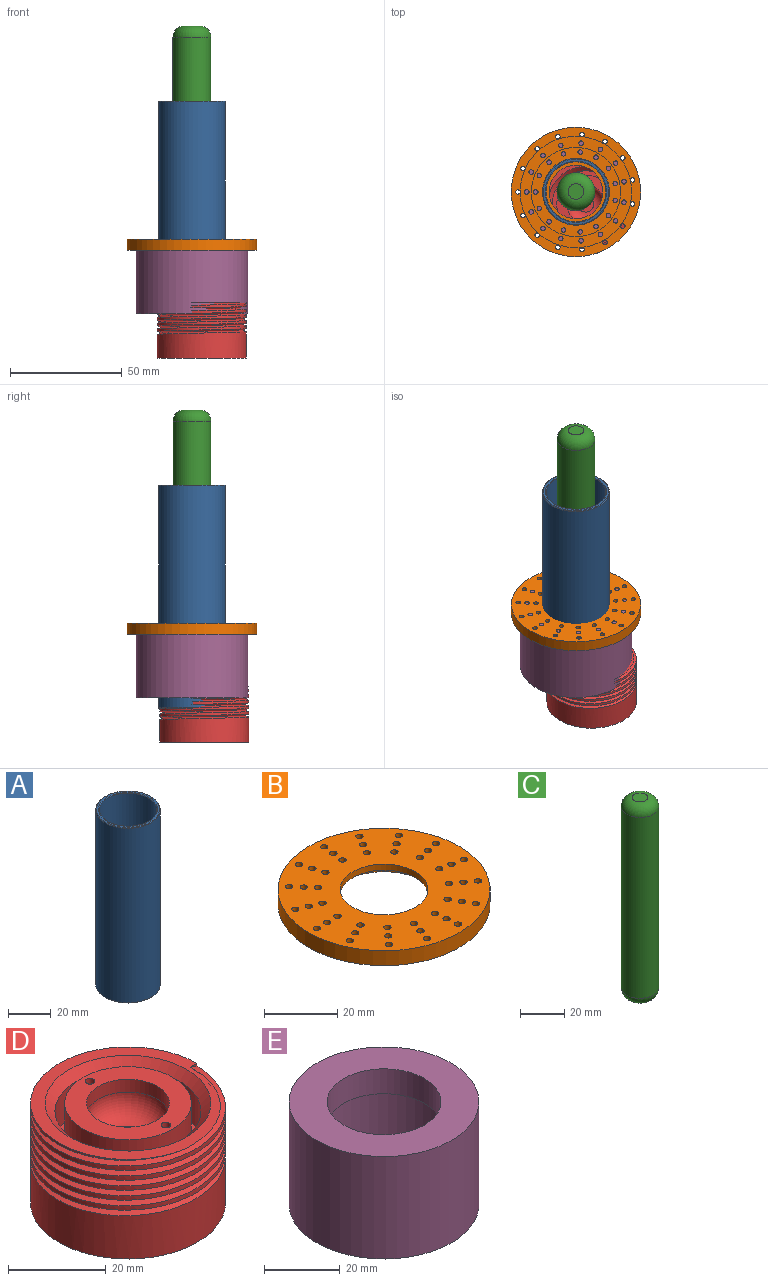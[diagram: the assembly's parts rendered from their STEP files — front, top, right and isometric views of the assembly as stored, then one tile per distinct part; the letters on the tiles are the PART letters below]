
ASSEMBLY  parts=5 mates=3
PART A: 8 faces, bbox 32.5x32.5x100 mm
  f0: cylinder r=13.4mm len=99.4mm, axis (0,0,-1), area 8369mm2, adj f4,f6
  f1: cylinder r=15mm len=99.4mm, axis (0,0,-1), area 9368.2mm2, adj f5,f7
  f2: plane 29.4x29.4mm, normal (0,0,1), area 89.2mm2, adj f6,f7
  f3: plane 29.4x29.4mm, normal (0,0,-1), area 89.2mm2, adj f4,f5
  f4: torus R=13.7mm, axis (0,0,1), area 40mm2, adj f0,f3
  f5: torus R=14.7mm, axis (0,0,1), area 44.1mm2, adj f1,f3
  f6: torus R=13.7mm, axis (0,0,1), area 40mm2, adj f0,f2
  f7: torus R=14.7mm, axis (0,0,1), area 44.1mm2, adj f1,f2
PART B: 51 faces, bbox 58x58x5 mm
  f0: cylinder r=12mm len=24mm, axis (0,0,1), area 150.8mm2, adj f2,f5
  f1: cylinder r=29mm len=58mm, axis (0,0,-1), area 911.1mm2, adj f2,f3
  f2: plane 58x58mm, normal (0,0,1), area 2048.3mm2, adj f0,f1,f6,f7,f8,f9,f10,f11
  f3: plane 58x58mm, normal (0,0,-1), area 1745.9mm2, adj f1,f4,f6,f7,f8,f9,f10,f11
  f4: cylinder r=15.5mm len=31mm, axis (0,0,-1), area 292.2mm2, adj f3,f5
  f5: plane 31x31mm, normal (0,0,-1), area 302.4mm2, adj f0,f4
  f6: cylinder r=1mm len=5mm, axis (0,0,1), area 31.4mm2, adj f2,f3
  f7: cylinder r=1mm len=5mm, axis (0,0,1), area 31.4mm2, adj f2,f3
  f8: cylinder r=1mm len=5mm, axis (0,0,1), area 31.4mm2, adj f2,f3
  f9: cylinder r=1mm len=5mm, axis (0,0,1), area 31.4mm2, adj f2,f3
  f10: cylinder r=1mm len=5mm, axis (0,0,1), area 31.4mm2, adj f2,f3
  f11: cylinder r=1mm len=5mm, axis (0,0,1), area 31.4mm2, adj f2,f3
  f12: cylinder r=1mm len=5mm, axis (0,0,1), area 31.4mm2, adj f2,f3
  f13: cylinder r=1mm len=5mm, axis (0,0,1), area 31.4mm2, adj f2,f3
  f14: cylinder r=1mm len=5mm, axis (0,0,1), area 31.4mm2, adj f2,f3
  f15: cylinder r=1mm len=5mm, axis (0,0,1), area 31.4mm2, adj f2,f3
  f16: cylinder r=1mm len=5mm, axis (0,0,1), area 31.4mm2, adj f2,f3
  f17: cylinder r=1mm len=5mm, axis (0,0,1), area 31.4mm2, adj f2,f3
  f18: cylinder r=1mm len=5mm, axis (0,0,1), area 31.4mm2, adj f2,f3
  f19: cylinder r=1mm len=5mm, axis (0,0,1), area 31.4mm2, adj f2,f3
  f20: cylinder r=1mm len=5mm, axis (0,0,1), area 31.4mm2, adj f2,f3
  f21: cylinder r=1mm len=5mm, axis (0,0,1), area 31.4mm2, adj f2,f3
  f22: cylinder r=1mm len=5mm, axis (0,0,1), area 31.4mm2, adj f2,f3
  f23: cylinder r=1mm len=5mm, axis (0,0,1), area 31.4mm2, adj f2,f3
  f24: cylinder r=1mm len=5mm, axis (0,0,1), area 31.4mm2, adj f2,f3
  f25: cylinder r=1mm len=5mm, axis (0,0,1), area 31.4mm2, adj f2,f3
  f26: cylinder r=1mm len=5mm, axis (0,0,1), area 31.4mm2, adj f2,f3
  f27: cylinder r=1mm len=5mm, axis (0,0,1), area 31.4mm2, adj f2,f3
  f28: cylinder r=1mm len=5mm, axis (0,0,1), area 31.4mm2, adj f2,f3
  f29: cylinder r=1mm len=5mm, axis (0,0,1), area 31.4mm2, adj f2,f3
  f30: cylinder r=1mm len=5mm, axis (0,0,1), area 31.4mm2, adj f2,f3
  f31: cylinder r=1mm len=5mm, axis (0,0,1), area 31.4mm2, adj f2,f3
  f32: cylinder r=1mm len=5mm, axis (0,0,1), area 31.4mm2, adj f2,f3
  f33: cylinder r=1mm len=5mm, axis (0,0,1), area 31.4mm2, adj f2,f3
  f34: cylinder r=1mm len=5mm, axis (0,0,1), area 31.4mm2, adj f2,f3
  f35: cylinder r=1mm len=5mm, axis (0,0,1), area 31.4mm2, adj f2,f3
  f36: cylinder r=1mm len=5mm, axis (0,0,1), area 31.4mm2, adj f2,f3
  f37: cylinder r=1mm len=5mm, axis (0,0,1), area 31.4mm2, adj f2,f3
  f38: cylinder r=1mm len=5mm, axis (0,0,1), area 31.4mm2, adj f2,f3
  f39: cylinder r=1mm len=5mm, axis (0,0,1), area 31.4mm2, adj f2,f3
  f40: cylinder r=1mm len=5mm, axis (0,0,1), area 31.4mm2, adj f2,f3
  f41: cylinder r=1mm len=5mm, axis (0,0,1), area 31.4mm2, adj f2,f3
  f42: cylinder r=1mm len=5mm, axis (0,0,1), area 31.4mm2, adj f2,f3
  f43: cylinder r=1mm len=5mm, axis (0,0,1), area 31.4mm2, adj f2,f3
  f44: cylinder r=1mm len=5mm, axis (0,0,1), area 31.4mm2, adj f2,f3
  f45: cylinder r=1mm len=5mm, axis (0,0,1), area 31.4mm2, adj f2,f3
  f46: cylinder r=1mm len=5mm, axis (0,0,1), area 31.4mm2, adj f2,f3
  f47: cylinder r=1mm len=5mm, axis (0,0,1), area 31.4mm2, adj f2,f3
  f48: cylinder r=1mm len=5mm, axis (0,0,1), area 31.4mm2, adj f2,f3
  f49: cylinder r=1mm len=5mm, axis (0,0,1), area 31.4mm2, adj f2,f3
  f50: cylinder r=1mm len=5mm, axis (0,0,1), area 31.4mm2, adj f2,f3
PART C: 7 faces, bbox 17x17x110 mm
  f0: cylinder r=8.5mm len=100mm, axis (0,0,-1), area 5340.7mm2, adj f3,f4
  f1: plane 7x7mm, normal (0,0,1), area 38.5mm2, adj f4
  f2: plane 7x7mm, normal (0,0,-1), area 33.6mm2, adj f3,f6
  f3: torus R=3.5mm, axis (0,0,1), area 329.8mm2, adj f0,f2
  f4: torus R=3.5mm, axis (0,0,1), area 329.8mm2, adj f0,f1
  f5: cone r=0mm half-angle=59deg, axis (0,0,-1), area 5.7mm2, adj f6
  f6: cylinder r=1.25mm len=6.5mm, axis (0,0,-1), area 51.1mm2, adj f2,f5
PART D: 27 faces, bbox 43.5x50.1x27.1 mm
  f0: cylinder r=20mm len=40mm, axis (0,0,-1), area 1327.1mm2, adj f1,f10,f23,f26
  f1: cylinder r=20mm len=40mm, axis (0,0,-1), area 138.9mm2, adj f0,f2,f25,f26
  f2: cylinder r=20mm len=40mm, axis (0,0,-1), area 138.7mm2, adj f1,f3,f25,f26
  f3: cylinder r=20mm len=40mm, axis (0,0,-1), area 138.8mm2, adj f2,f4,f25,f26
  f4: cylinder r=20mm len=40mm, axis (0,0,-1), area 139mm2, adj f3,f5,f25,f26
  f5: cylinder r=20mm len=40mm, axis (0,0,-1), area 138.8mm2, adj f4,f6,f25,f26
  f6: cylinder r=20mm len=40mm, axis (0,0,-1), area 81mm2, adj f5,f7,f24,f25
  f7: plane 40.94x40.75mm, normal (0,0,1), area 315.2mm2, adj f6,f18,f24,f25,f26
  f8: cylinder r=1mm len=16.94mm, axis (0,0,1), area 106.4mm2, adj f14,f21
  f9: cylinder r=1mm len=16.94mm, axis (0,0,1), area 106.4mm2, adj f14,f19
  f10: plane 40x40mm, normal (0,0,-1), area 1228.9mm2, adj f0,f20,f22
  f11: cylinder r=13mm len=26mm, axis (0,0,1), area 816.8mm2, adj f13,f14
  f12: cylinder r=15mm len=30mm, axis (0,0,1), area 754mm2, adj f13,f18
  f13: plane 30x30mm, normal (0,0,1), area 175.9mm2, adj f11,f12
  f14: plane 26x26mm, normal (0,0,1), area 297.7mm2, adj f8,f9,f11,f15
  f15: cylinder r=8.5mm len=17mm, axis (0,0,1), area 170.9mm2, adj f14,f17
  f16: plane 7x7mm, normal (0,0,1), area 38.5mm2, adj f17
  f17: torus R=3.5mm, axis (0,0,1), area 329.8mm2, adj f15,f16
  f18: cone r=15mm half-angle=45deg, axis (0,0,1), area 284.3mm2, adj f7,f12
  f19: cone r=0mm half-angle=59deg, axis (0,0,-1), area 12.5mm2, adj f9,f20
  f20: cylinder r=2.1mm len=7.4mm, axis (0,0,-1), area 97.6mm2, adj f10,f19
  f21: cone r=0mm half-angle=59deg, axis (0,0,-1), area 12.5mm2, adj f8,f22
  f22: cylinder r=2.1mm len=7.4mm, axis (0,0,-1), area 97.6mm2, adj f10,f21
  f23: plane 1.9x1.4mm, normal (0,1,0), area 1.3mm2, adj f0,f25,f26
  f24: plane 1.84x0.69mm, normal (0,-1,0), area 0.6mm2, adj f6,f7,f26
  f25: bspline ~49.18x42.59mm, area 1415.2mm2, adj f1,f2,f3,f4,f5,f6,f7,f23
  f26: bspline ~49.18x42.59mm, area 1456.3mm2, adj f0,f1,f2,f3,f4,f5,f7,f23
PART E: 6 faces, bbox 50x50x33 mm
  f0: cylinder r=20mm len=40mm, axis (0,0,-1), area 3141.6mm2, adj f2,f3
  f1: cylinder r=25mm len=50mm, axis (0,0,-1), area 5183.6mm2, adj f2,f5
  f2: plane 50x50mm, normal (0,0,-1), area 706.9mm2, adj f0,f1
  f3: plane 40x40mm, normal (0,0,-1), area 549.8mm2, adj f0,f4
  f4: cylinder r=15mm len=30mm, axis (0,0,-1), area 754mm2, adj f3,f5
  f5: plane 50x50mm, normal (0,0,1), area 1256.6mm2, adj f1,f4
PLACE A rot(axis=(0,0,1),4.4deg) t=(16.31,-25.1,6.32)mm
PLACE B t=(16.31,-25.1,39.43)mm
PLACE C rot(axis=(0,0,-1),19.2deg) t=(16.31,-25.1,29.98)mm
PLACE D t=(20.72,-30.55,-8.86)mm fixed
PLACE E rot(axis=(0.27,-0.96,0),180deg) t=(16.31,-25.1,43.96)mm
MATE cylindrical B.f0 <-> A.f1  axis (0,0,1) through (16.31,-25.1,44.43)mm
MATE cylindrical C.f0 <-> A.f0  axis (0,0,-1) through (16.31,-25.1,84.98)mm
MATE cylindrical E.f1 <-> A.f1  axis (0,0,1) through (16.31,-25.1,27.46)mm
